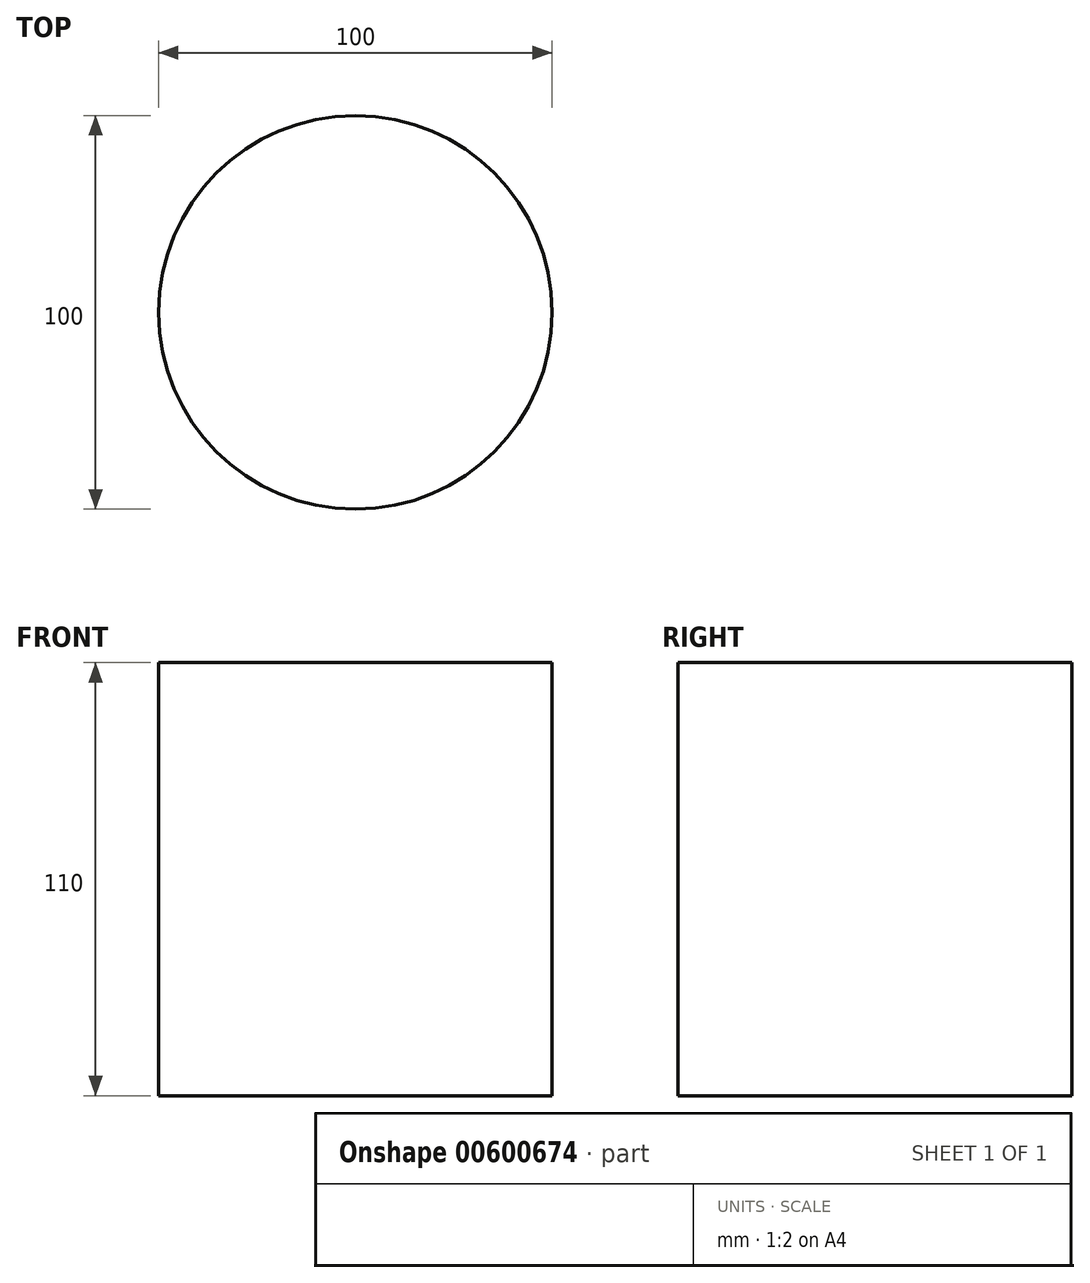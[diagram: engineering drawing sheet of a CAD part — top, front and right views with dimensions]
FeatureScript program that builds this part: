
annotation { "Feature Type Name" : "Feature", "Feature Type Description" : "" }
export const myFeature = defineFeature(function(context is Context, id is Id, definition is map)
    precondition{}
    {
        {
            var Q0;
            Q0=qCreatedBy(makeId("Top.planeOp"),FACE);
            var sketch = newSketch(context, id + "F0", { "sketchPlane" : qUnion([Q0])});
            skCircle(sketch, "E0", {"center": v(0, 2.26) * mm, "radius": 50 * mm});
            skSolve(sketch);
        }
        {
            var Q0;
            Q0=makeQuery(id+"F0.imprint","IMPRINT",FACE,{"disambiguationData":[TD([[makeQuery(id+"F0.imprint","IMPRINT",EDGE,{"derivedFrom":sQuery(id+"F0.wireOp",EDGE,"E0")}),1.0]])]});
            extrude(context, id + "F1", {"entities" : qUnion([Q0]), "depth" : 110 * mm, "offsetDistance" : 25 * mm});
        }
    });
